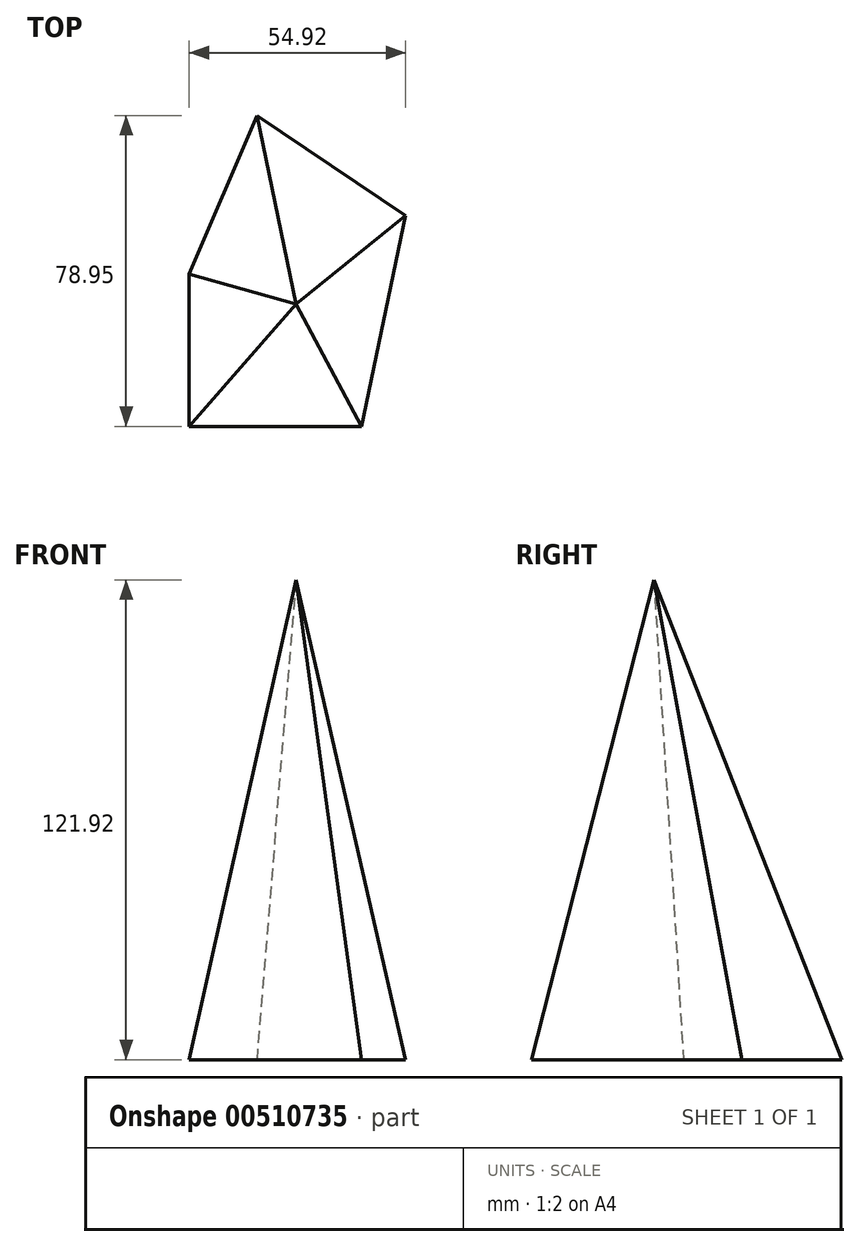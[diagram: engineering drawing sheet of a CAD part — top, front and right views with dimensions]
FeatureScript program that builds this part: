
annotation { "Feature Type Name" : "Feature", "Feature Type Description" : "" }
export const myFeature = defineFeature(function(context is Context, id is Id, definition is map)
    precondition{}
    {
        {
            var Q0;
            Q0=qCreatedBy(makeId("Top.planeOp"),FACE);
            var sketch = newSketch(context, id + "F0", { "sketchPlane" : qUnion([Q0])});
            skLineSegment(sketch, "E0", {"start": v(-58.83, 12.05) * mm, "end": v(-41.67, 52.38) * mm});
            skLineSegment(sketch, "E1", {"start": v(-41.67, 52.38) * mm, "end": v(-3.91, 26.93) * mm});
            skLineSegment(sketch, "E2", {"start": v(-58.83, 12.05) * mm, "end": v(-58.83, -26.57) * mm});
            skLineSegment(sketch, "E3", {"start": v(-58.83, -26.57) * mm, "end": v(-15.11, -26.57) * mm});
            skLineSegment(sketch, "E4", {"start": v(-15.11, -26.57) * mm, "end": v(-3.91, 26.93) * mm});
            skSolve(sketch);
        }
        {
            var Q0;
            Q0=qCreatedBy(makeId("Top.planeOp"),FACE);
            cPlane(context, id + "F1", {"entities" : qUnion([Q0]), "cplaneType" : CPlaneType.OFFSET, "offset" : 121.92 * mm, "width" : 152.4 * mm, "height" : 152.4 * mm});
        }
        {
            var Q0;
            Q0=qCreatedBy(id+"F1.planeOp",FACE);
            var sketch = newSketch(context, id + "F2", { "sketchPlane" : qUnion([Q0])});
            skPoint(sketch, "E5", {"position": v(-31.77, 4.52) * mm});
            skSolve(sketch);
        }
        {
            var Q0;
            Q0=sQuery(id+"F2.wireOp",VERTEX,"E5");
            var Q1;
            Q1=makeQuery(id+"F0.imprint","IMPRINT",FACE,{"disambiguationData":[TD([[makeQuery(id+"F0.imprint","IMPRINT",EDGE,{"derivedFrom":sQuery(id+"F0.wireOp",EDGE,"E0")}),-1.0]])]});
            loft(context, id + "F3", {"sheetProfilesArray" : [{ "sheetProfileEntities" : qUnion([Q0]) }, { "sheetProfileEntities" : qUnion([Q1]) }]});
        }
    });
